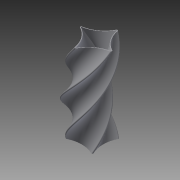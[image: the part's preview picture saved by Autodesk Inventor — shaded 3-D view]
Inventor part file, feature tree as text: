
AUTODESK INVENTOR PART (.ipt)
format: ipt  version: 2013 (Build 170138000, 138)  size: 528,384 bytes
history: native  units: mm
features: fillet x2, helix x1, shell x1, sketch x1
ambient origin geometry x8: Origin, YZ Plane, XZ Plane, XY Plane, X Axis, Y Axis, Z Axis, Center Point
bodies: Solid1 (feature_tree)
feature tree (5):
  helix  "Coil1"  [1 undecoded]
  fillet  "Fillet1"  Radius=1.25mm
  fillet  "Fillet2"  Radius=1.0mm
  shell  "Shell1"  [1 undecoded]
  sketch  "Sketch1"  dims[d1=10.0mm d2=150.0mm d3=6.0mm d4=0.0mm d5=90.0deg d6=90.0deg d7=0.0mm d8=0.0mm d9=1.25mm d10=1.25mm d11=1.0mm]
note: 2 required parameter values undecoded (feature->parameter linkage not recoverable at this tier; creation-order binding heuristic only, values carry confidence <= 0.55)
